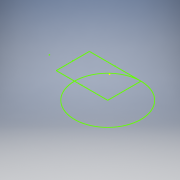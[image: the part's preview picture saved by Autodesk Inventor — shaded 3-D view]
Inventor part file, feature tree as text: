
AUTODESK INVENTOR PART (.ipt)
format: ipt  version: 2018 (Build 220112000, 112)  size: 85,504 bytes
history: native  units: in
note: dims shown in document units (in); Inventor stores cm internally (conversion verified against a paired STEP export)
features: sketch x1
ambient origin geometry x8: Origin, YZ Plane, XZ Plane, XY Plane, X Axis, Y Axis, Z Axis, Center Point
feature tree (1):
  sketch  "Sketch1"
